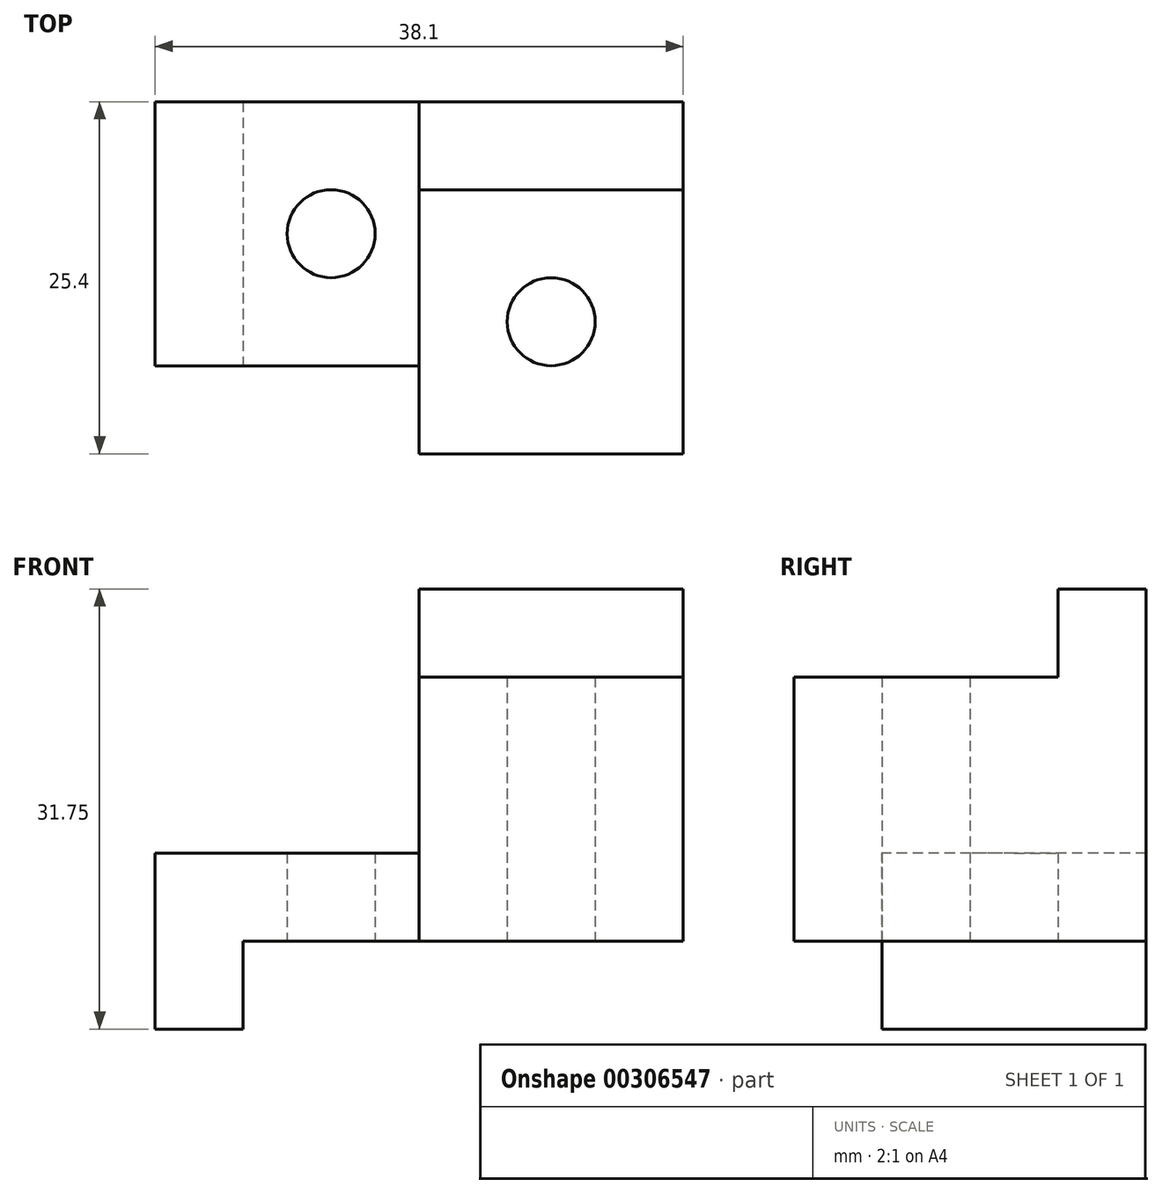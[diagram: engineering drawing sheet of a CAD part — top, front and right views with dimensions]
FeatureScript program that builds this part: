
annotation { "Feature Type Name" : "Feature", "Feature Type Description" : "" }
export const myFeature = defineFeature(function(context is Context, id is Id, definition is map)
    precondition{}
    {
        {
            var Q0;
            Q0=qCreatedBy(makeId("Front.planeOp"),FACE);
            var sketch = newSketch(context, id + "F0", { "sketchPlane" : qUnion([Q0])});
            skLineSegment(sketch, "E0", {"start": v(0, 0) * mm, "end": v(6.35, 0) * mm});
            skLineSegment(sketch, "E1", {"start": v(6.35, 0) * mm, "end": v(6.35, 6.35) * mm});
            skLineSegment(sketch, "E2", {"start": v(6.35, 6.35) * mm, "end": v(19.05, 6.35) * mm});
            skLineSegment(sketch, "E3", {"start": v(19.05, 6.35) * mm, "end": v(19.05, 12.7) * mm});
            skLineSegment(sketch, "E4", {"start": v(19.05, 12.7) * mm, "end": v(0, 12.7) * mm});
            skLineSegment(sketch, "E5", {"start": v(0, 12.7) * mm, "end": v(0, 0) * mm});
            skLineSegment(sketch, "E6", {"start": v(19.05, 6.35) * mm, "end": v(38.1, 6.35) * mm});
            skLineSegment(sketch, "E7", {"start": v(38.1, 6.35) * mm, "end": v(38.1, 25.4) * mm});
            skLineSegment(sketch, "E8", {"start": v(38.1, 25.4) * mm, "end": v(19.05, 25.4) * mm});
            skLineSegment(sketch, "E9", {"start": v(19.05, 25.4) * mm, "end": v(19.05, 12.7) * mm});
            skLineSegment(sketch, "E10", {"start": v(19.05, 25.4) * mm, "end": v(19.05, 31.75) * mm});
            skLineSegment(sketch, "E11", {"start": v(19.05, 31.75) * mm, "end": v(38.1, 31.75) * mm});
            skLineSegment(sketch, "E12", {"start": v(38.1, 31.75) * mm, "end": v(38.1, 25.4) * mm});
            skSolve(sketch);
        }
        {
            var Q0;
            Q0=makeQuery(id+"F0.imprint","IMPRINT",FACE,{"disambiguationData":[TD([[makeQuery(id+"F0.imprint","IMPRINT",EDGE,{"derivedFrom":sQuery(id+"F0.wireOp",EDGE,"E8")}),-1.0]])]});
            var Q1;
            Q1=makeQuery(id+"F0.imprint","IMPRINT",FACE,{"disambiguationData":[TD([[makeQuery(id+"F0.imprint","IMPRINT",EDGE,{"derivedFrom":sQuery(id+"F0.wireOp",EDGE,"E3")}),-1.0]])]});
            extrude(context, id + "F1", {"entities" : qUnion([Q0, Q1]), "oppositeDirection" : true, "depth" : 25.4 * mm});
        }
        {
            var Q0;
            Q0=makeQuery(id+"F0.imprint","IMPRINT",FACE,{"disambiguationData":[TD([[makeQuery(id+"F0.imprint","IMPRINT",EDGE,{"derivedFrom":sQuery(id+"F0.wireOp",EDGE,"E0")}),1.0]])]});
            extrude(context, id + "F2", {"entities" : qUnion([Q0]), "operationType" : NewBodyOperationType.ADD, "oppositeDirection" : true, "depth" : 25.4 * mm, "hasSecondDirection" : true, "secondDirectionOppositeDirection" : true, "secondDirectionDepth" : 6.35 * mm});
        }
        {
            var Q0;
            Q0=makeQuery(id+"F1.opExtrude","SWEPT_FACE",FACE,{"disambiguationData":[OSD([sQuery(id+"F0.wireOp",EDGE,"E7"),sQuery(id+"F0.wireOp",EDGE,"E12")])]});
            var sketch = newSketch(context, id + "F3", { "sketchPlane" : qUnion([Q0])});
            skSolve(sketch);
        }
        {
            var Q0;
            {var subQ0=sQuery(id+"F0.wireOp",EDGE,"E7");Q0=makeQuery(id+"F3.imprint","IMPRINT",FACE,{"disambiguationData":[TD([[makeQuery(id+"F3.imprint","IMPRINT",EDGE,{"derivedFrom":makeQuery(id+"F1.opExtrude","SWEPT_EDGE",EDGE,{"disambiguationData":[OSD([sQuery(id+"F0.wireOp",EDGE,"E6"),subQ0])]})}),-1.0]])]});}
            var sketch = newSketch(context, id + "F4", { "sketchPlane" : qUnion([Q0])});
            skLineSegment(sketch, "E13", {"start": v(0, 31.75) * mm, "end": v(19.05, 31.75) * mm});
            skLineSegment(sketch, "E14", {"start": v(19.05, 31.75) * mm, "end": v(19.05, 25.4) * mm});
            skLineSegment(sketch, "E15", {"start": v(19.05, 25.4) * mm, "end": v(0, 25.4) * mm});
            skLineSegment(sketch, "E16", {"start": v(0, 25.4) * mm, "end": v(0, 31.75) * mm});
            skSolve(sketch);
        }
        {
            var Q0;
            Q0 = qSketchRegion(id + "F4", true);
            extrude(context, id + "F5", {"entities" : qUnion([Q0]), "operationType" : NewBodyOperationType.REMOVE, "endBound" : BoundingType.THROUGH_ALL, "oppositeDirection" : true, "depth" : 25.4 * mm});
        }
        {
            var Q0;
            Q0=qCreatedBy(makeId("Top.planeOp"),FACE);
            var sketch = newSketch(context, id + "F6", { "sketchPlane" : qUnion([Q0])});
            skCircle(sketch, "E17", {"center": v(12.7, 15.88) * mm, "radius": 3.18 * mm});
            skCircle(sketch, "E18", {"center": v(28.58, 9.53) * mm, "radius": 3.18 * mm});
            skSolve(sketch);
        }
        {
            var Q0;
            Q0 = qSketchRegion(id + "F6", true);
            extrude(context, id + "F7", {"entities" : qUnion([Q0]), "operationType" : NewBodyOperationType.REMOVE, "endBound" : BoundingType.THROUGH_ALL, "depth" : 25.4 * mm});
        }
    });
